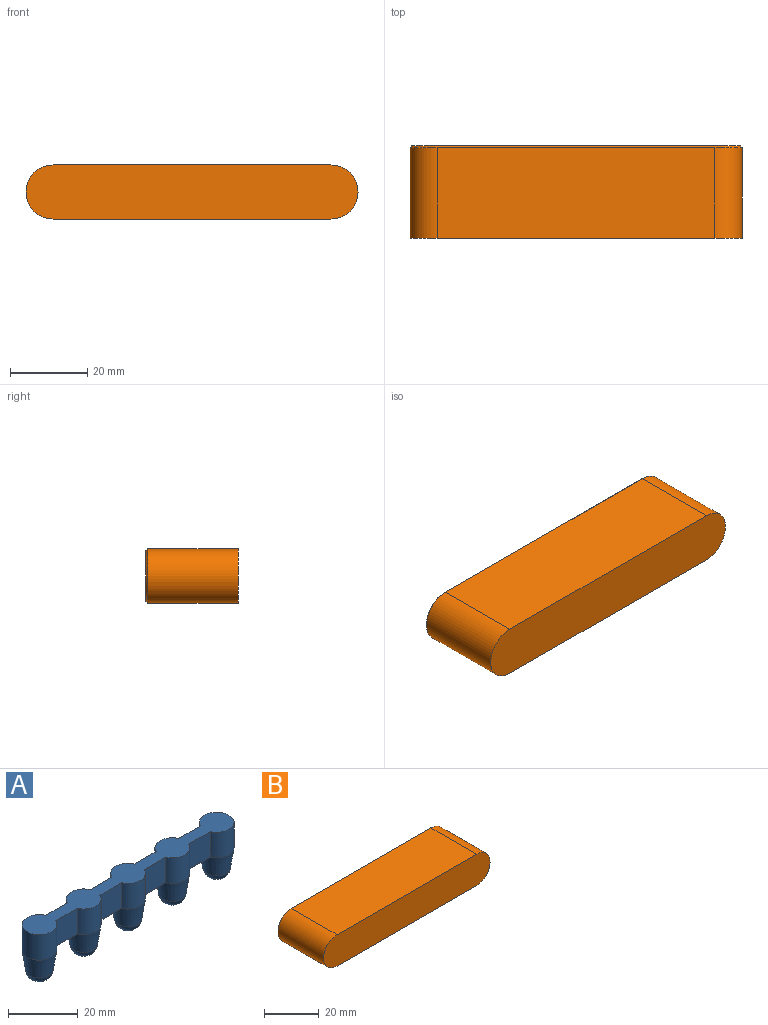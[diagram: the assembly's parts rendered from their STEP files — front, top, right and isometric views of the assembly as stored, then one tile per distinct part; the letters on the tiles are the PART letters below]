
ASSEMBLY  parts=2 mates=1
PART A: 36 faces, bbox 82x10x19 mm
  f0: plane 9x8.84mm, normal (0,1,0), area 79.5mm2, adj f8,f11,f19,f35
  f1: plane 9x8.84mm, normal (0,1,0), area 79.5mm2, adj f6,f8,f12,f35
  f2: plane 9x8.84mm, normal (0,1,0), area 79.5mm2, adj f4,f6,f15,f35
  f3: plane 9x8.84mm, normal (0,1,0), area 79.5mm2, adj f19,f21,f23,f35
  f4: cylinder r=5mm len=10mm, axis (0,0,-1), area 245.7mm2, adj f2,f14,f27,f35
  f5: cylinder r=5mm len=9.17mm, axis (0,0,-1), area 104.3mm2, adj f13,f14,f26,f35
  f6: cylinder r=5mm len=9.17mm, axis (0,0,-1), area 104.3mm2, adj f1,f2,f26,f35
  f7: cylinder r=5mm len=9.17mm, axis (0,0,-1), area 104.3mm2, adj f10,f13,f25,f35
  f8: cylinder r=5mm len=9.17mm, axis (0,0,-1), area 104.3mm2, adj f0,f1,f25,f35
  f9: cylinder r=5mm len=9.17mm, axis (0,0,-1), area 104.3mm2, adj f10,f22,f29,f35
  f10: plane 9x8.84mm, normal (0,-1,0), area 79.5mm2, adj f7,f9,f11,f35
  f11: plane 8.84x4mm, normal (0,0,-1), area 33.1mm2, adj f0,f10,f25,f29
  f12: plane 8.84x4mm, normal (0,0,-1), area 33.1mm2, adj f1,f13,f25,f26
  f13: plane 9x8.84mm, normal (0,-1,0), area 79.5mm2, adj f5,f7,f12,f35
  f14: plane 9x8.84mm, normal (0,-1,0), area 79.5mm2, adj f4,f5,f15,f35
  f15: plane 8.84x4mm, normal (0,0,-1), area 33.1mm2, adj f2,f14,f26,f27
  f16: plane 0.97x0.97mm, normal (0,0,-1), area 0.7mm2, adj f32
  f17: plane 0.97x0.97mm, normal (0,0,-1), area 0.7mm2, adj f33
  f18: plane 0.97x0.97mm, normal (0,0,-1), area 0.7mm2, adj f34
  f19: cylinder r=5mm len=9.17mm, axis (0,0,-1), area 104.3mm2, adj f0,f3,f29,f35
  f20: plane 0.97x0.97mm, normal (0,0,-1), area 0.7mm2, adj f30
  f21: plane 8.84x4mm, normal (0,0,-1), area 33.1mm2, adj f3,f22,f28,f29
  f22: plane 9x8.84mm, normal (0,-1,0), area 79.5mm2, adj f9,f21,f23,f35
  f23: cylinder r=5mm len=10mm, axis (0,0,-1), area 245.7mm2, adj f3,f22,f28,f35
  f24: plane 0.97x0.97mm, normal (0,0,-1), area 0.7mm2, adj f31
  f25: cone r=5mm half-angle=8.5deg, axis (0,0,1), area 199.5mm2, adj f7,f8,f11,f12,f34
  f26: cone r=5mm half-angle=8.5deg, axis (0,0,1), area 199.5mm2, adj f5,f6,f12,f15,f33
  f27: cone r=5mm half-angle=8.5deg, axis (0,0,1), area 199.5mm2, adj f4,f15,f32
  f28: cone r=3.5mm half-angle=8.5deg, axis (0,0,1), area 199.5mm2, adj f21,f23,f31
  f29: cone r=3.5mm half-angle=8.5deg, axis (0,0,1), area 199.5mm2, adj f9,f11,f19,f21,f30
  f30: torus R=0.49mm, axis (0,0,1), area 80.7mm2, adj f20,f29
  f31: torus R=0.49mm, axis (0,0,1), area 80.7mm2, adj f24,f28
  f32: torus R=0.49mm, axis (0,0,1), area 80.7mm2, adj f16,f27
  f33: torus R=0.49mm, axis (0,0,1), area 80.7mm2, adj f17,f26
  f34: torus R=0.49mm, axis (0,0,1), area 80.7mm2, adj f18,f25
  f35: plane 82x10mm, normal (0,0,1), area 525.1mm2, adj f0,f1,f2,f3,f4,f5,f6,f7
PART B: 40 faces, bbox 86x24x14 mm
  f0: cylinder r=5mm len=10mm, axis (0,1,0), area 245.7mm2, adj f8,f28,f29,f30
  f1: cylinder r=5mm len=9.17mm, axis (0,-1,0), area 104.3mm2, adj f10,f26,f28,f30
  f2: cylinder r=5mm len=9.17mm, axis (0,-1,0), area 104.3mm2, adj f10,f25,f29,f30
  f3: cylinder r=5mm len=9.17mm, axis (0,1,0), area 104.3mm2, adj f12,f23,f26,f30
  f4: cylinder r=5mm len=9.17mm, axis (0,1,0), area 104.3mm2, adj f12,f22,f25,f30
  f5: cylinder r=5mm len=9.17mm, axis (0,1,0), area 104.3mm2, adj f14,f20,f23,f30
  f6: cylinder r=5mm len=9.17mm, axis (0,1,0), area 104.3mm2, adj f14,f19,f22,f30
  f7: cylinder r=5mm len=10mm, axis (0,1,0), area 245.7mm2, adj f16,f19,f20,f30
  f8: cone r=5mm half-angle=9deg, axis (0,1,0), area 188.6mm2, adj f0,f9,f27
  f9: sphere r=4mm, area 84.8mm2, adj f8
  f10: cone r=5mm half-angle=9deg, axis (0,1,0), area 188.6mm2, adj f1,f2,f11,f24,f27
  f11: sphere r=4mm, area 84.8mm2, adj f10
  f12: cone r=5mm half-angle=9deg, axis (0,1,0), area 188.6mm2, adj f3,f4,f13,f21,f24
  f13: sphere r=4mm, area 84.8mm2, adj f12
  f14: cone r=5mm half-angle=9deg, axis (0,1,0), area 188.6mm2, adj f5,f6,f15,f18,f21
  f15: sphere r=4mm, area 84.8mm2, adj f14
  f16: cone r=5mm half-angle=9deg, axis (0,1,0), area 188.6mm2, adj f7,f17,f18
  f17: sphere r=4mm, area 84.8mm2, adj f16
  f18: plane 8.84x4mm, normal (0,1,0), area 33.1mm2, adj f14,f16,f19,f20
  f19: plane 9x8.84mm, normal (0,0,-1), area 79.5mm2, adj f6,f7,f18,f30
  f20: plane 9x8.84mm, normal (0,0,1), area 79.5mm2, adj f5,f7,f18,f30
  f21: plane 8.84x4mm, normal (0,1,0), area 33.1mm2, adj f12,f14,f22,f23
  f22: plane 9x8.84mm, normal (0,0,-1), area 79.5mm2, adj f4,f6,f21,f30
  f23: plane 9x8.84mm, normal (0,0,1), area 79.5mm2, adj f3,f5,f21,f30
  f24: plane 8.84x4mm, normal (0,1,0), area 33.1mm2, adj f10,f12,f25,f26
  f25: plane 9x8.84mm, normal (0,0,-1), area 79.5mm2, adj f2,f4,f24,f30
  f26: plane 9x8.84mm, normal (0,0,1), area 79.5mm2, adj f1,f3,f24,f30
  f27: plane 8.84x4mm, normal (0,1,0), area 33.1mm2, adj f8,f10,f28,f29
  f28: plane 9x8.84mm, normal (0,0,1), area 79.5mm2, adj f0,f1,f27,f30
  f29: plane 9x8.84mm, normal (0,0,-1), area 79.5mm2, adj f0,f2,f27,f30
  f30: plane 85x13mm, normal (0,1,0), area 543.7mm2, adj f0,f1,f2,f3,f4,f5,f6,f7
  f31: plane 86x14mm, normal (0,-1,0), area 1161.9mm2, adj f32,f33,f34,f35
  f32: cylinder r=7mm len=23.5mm, axis (0,1,0), area 516.8mm2, adj f31,f34,f35,f38
  f33: cylinder r=7mm len=23.5mm, axis (0,1,0), area 516.8mm2, adj f31,f34,f35,f37
  f34: plane 72x23.5mm, normal (0,0,-1), area 1692mm2, adj f31,f32,f33,f39
  f35: plane 72x23.5mm, normal (0,0,1), area 1692mm2, adj f31,f32,f33,f36
  f36: plane 72x0.5mm, normal (0,0.71,0.71), area 50.9mm2, adj f30,f35,f37,f38
  f37: cone r=7mm half-angle=45deg, axis (0,-1,0), area 15mm2, adj f30,f33,f36,f39
  f38: cone r=7mm half-angle=45deg, axis (0,-1,0), area 15mm2, adj f30,f32,f36,f39
  f39: plane 72x0.5mm, normal (0,0.71,-0.71), area 50.9mm2, adj f30,f34,f37,f38
PLACE A rot(axis=(-1,0,0),90deg) t=(-18.69,-3.81,-24.03)mm
PLACE B t=(-18.69,-8.81,-24.03)mm
MATE fastened A.f23 <-> B.f7  axis (0,1,0) through (17.31,-14.81,-24.03)mm
